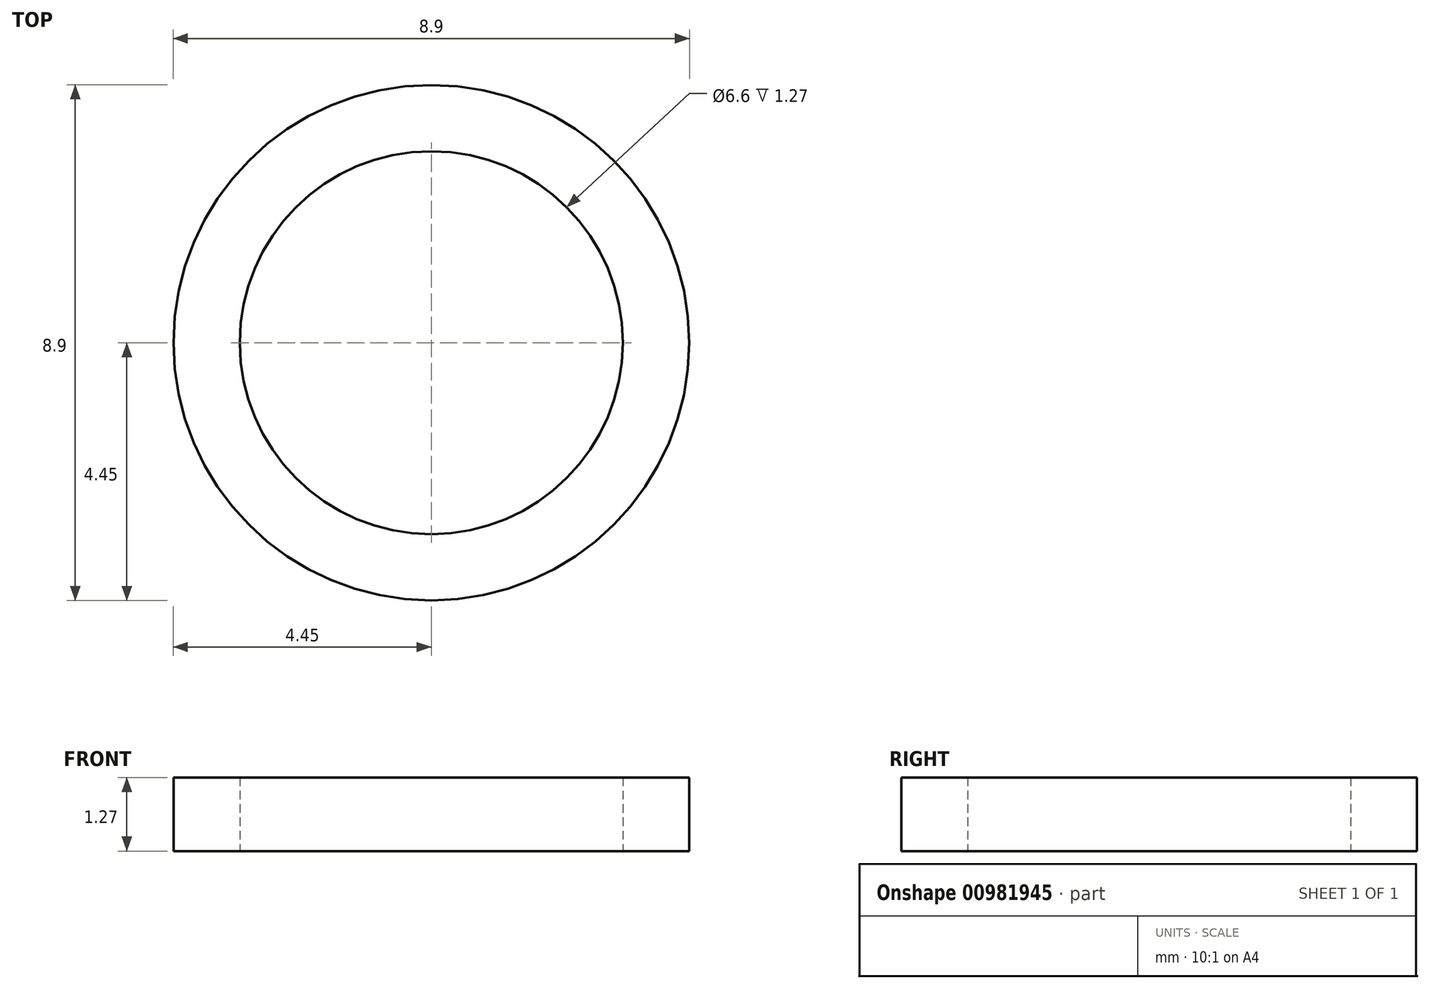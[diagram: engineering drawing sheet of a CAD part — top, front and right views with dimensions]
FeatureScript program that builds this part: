
annotation { "Feature Type Name" : "Feature", "Feature Type Description" : "" }
export const myFeature = defineFeature(function(context is Context, id is Id, definition is map)
    precondition{}
    {
        {
            var Q0;
            Q0=qCreatedBy(makeId("Top.planeOp"),FACE);
            var sketch = newSketch(context, id + "F0", { "sketchPlane" : qUnion([Q0])});
            skCircle(sketch, "E0", {"center": v(0, 0) * mm, "radius": 4.45 * mm});
            skCircle(sketch, "E1", {"center": v(0, 0) * mm, "radius": 3.3 * mm});
            skSolve(sketch);
        }
        {
            var Q0;
            Q0=qSketchRegion(id+"F0",true);
            extrude(context, id + "F1", {"entities" : qUnion([Q0]), "depth" : 1.27 * mm, "offsetDistance" : 25.4 * mm});
        }
    });
